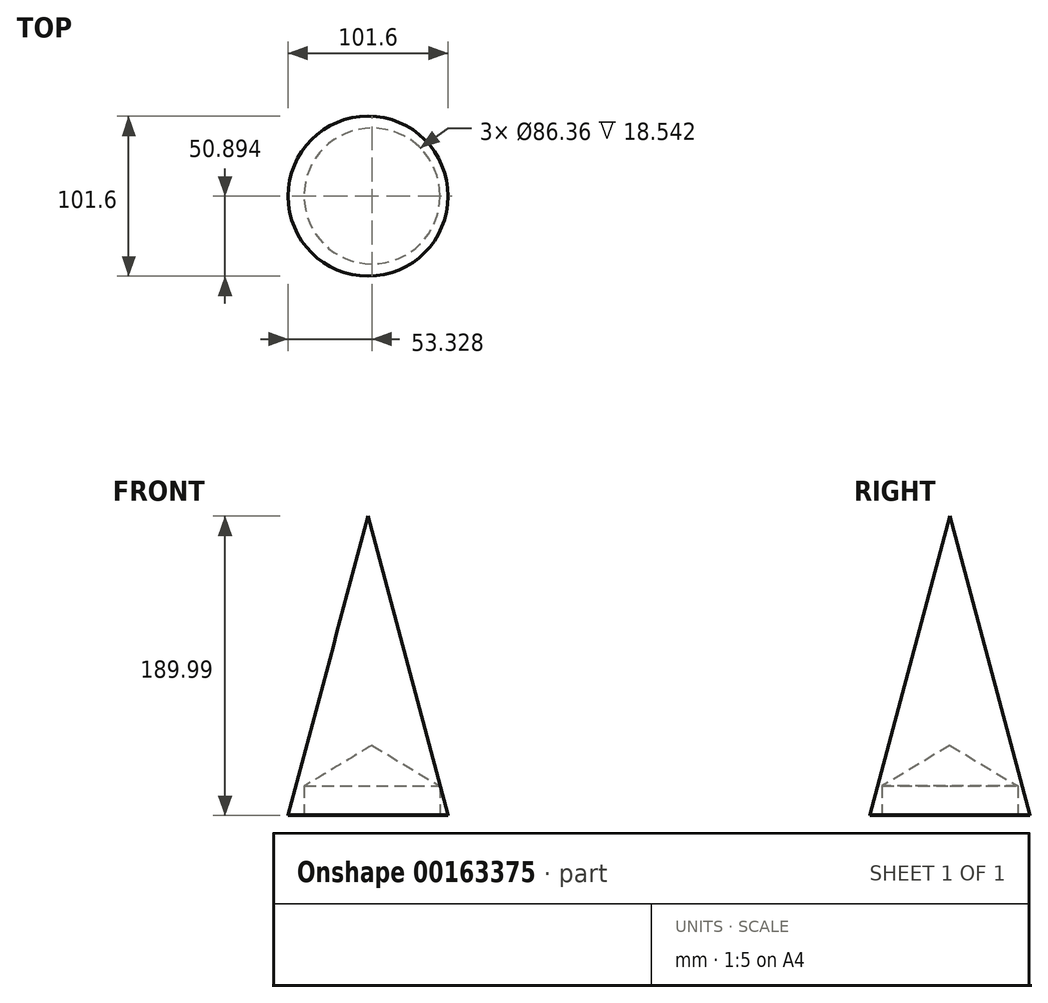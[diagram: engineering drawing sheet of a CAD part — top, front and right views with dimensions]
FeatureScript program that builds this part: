
annotation { "Feature Type Name" : "Feature", "Feature Type Description" : "" }
export const myFeature = defineFeature(function(context is Context, id is Id, definition is map)
    precondition{}
    {
        {
            var Q0;
            Q0=qCreatedBy(makeId("Top.planeOp"),FACE);
            var sketch = newSketch(context, id + "F0", { "sketchPlane" : qUnion([Q0])});
            skCircle(sketch, "E0", {"center": v(-50.35, 45.87) * mm, "radius": 50.8 * mm});
            skSolve(sketch);
        }
        {
            var Q0;
            Q0=makeQuery(id+"F0.imprint","IMPRINT",FACE,{"disambiguationData":[TD([[makeQuery(id+"F0.imprint","IMPRINT",EDGE,{"derivedFrom":sQuery(id+"F0.wireOp",EDGE,"E0")}),1.0]])]});
            extrude(context, id + "F1", {"entities" : qUnion([Q0]), "depth" : 190 * mm});
        }
        {
            var Q0;
            Q0=makeQuery(id+"F1.opExtrude","CAP_FACE",FACE,{"disambiguationData":[OSD([sQuery(id+"F0.wireOp",EDGE,"E0")])],"isStart":false});
            chamfer(context, id + "F2", {"entities" : qUnion([Q0]), "chamferType" : ChamferType.OFFSET_ANGLE, "width" : 50.8 * mm, "oppositeDirection" : false, "angle" : 75 * degree, "tangentPropagation" : true});
        }
        {
            var Q0;
            Q0=makeQuery(id+"F1.opExtrude","CAP_FACE",FACE,{"disambiguationData":[OSD([sQuery(id+"F0.wireOp",EDGE,"E0")])],"isStart":true});
            var sketch = newSketch(context, id + "F3", { "sketchPlane" : qUnion([Q0])});
            skPoint(sketch, "E1", {"position": v(-47.82, -45.96) * mm});
            skSolve(sketch);
        }
        {
            var Q0;
            Q0=sQuery(id+"F3.wireOp",VERTEX,"E1");
            var Q1;
            Q1=makeQuery(id+"F1.opExtrude","SWEPT_BODY",BODY,{"disambiguationData":[OSD([sQuery(id+"F0.wireOp",EDGE,"E0")])]});
            hole(context, id + "F4", {"style" : HoleStyle.SIMPLE, "endStyle" : HoleEndStyle.BLIND, "holeDiameter" : 86.36 * mm, "holeDepth" : 18.54 * mm, "locations" : qUnion([Q0]), "scope" : qUnion([Q1])});
        }
    });
